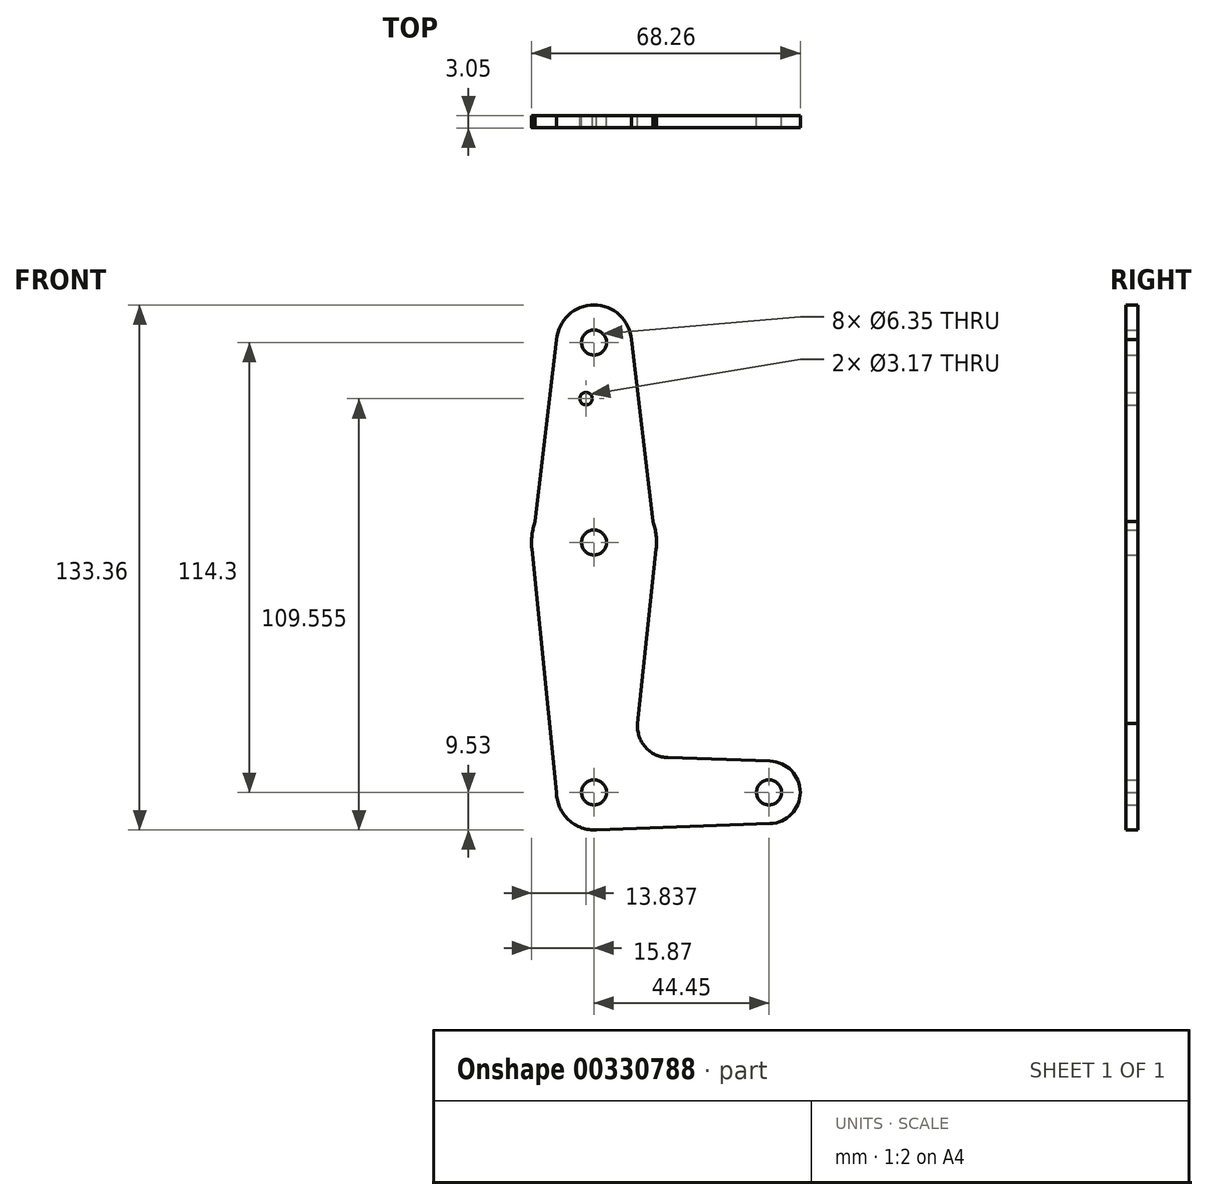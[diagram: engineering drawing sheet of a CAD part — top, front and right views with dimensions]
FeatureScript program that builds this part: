
annotation { "Feature Type Name" : "Feature", "Feature Type Description" : "" }
export const myFeature = defineFeature(function(context is Context, id is Id, definition is map)
    precondition{}
    {
        {
            var Q0;
            Q0=qCreatedBy(makeId("Front.planeOp"),FACE);
            var sketch = newSketch(context, id + "F0", { "sketchPlane" : qUnion([Q0])});
            skLineSegment(sketch, "E0", {"start": v(0, 0) * mm, "end": v(0, 114.3) * mm, "construction": true});
            skLineSegment(sketch, "E1", {"start": v(0, 0) * mm, "end": v(44.45, 0) * mm, "construction": true});
            skCircle(sketch, "E2", {"center": v(0, 114.3) * mm, "radius": 9.53 * mm});
            skCircle(sketch, "E3", {"center": v(0, 63.5) * mm, "radius": 15.88 * mm});
            skCircle(sketch, "E4", {"center": v(0, 0) * mm, "radius": 9.53 * mm});
            skCircle(sketch, "E5", {"center": v(44.45, 0) * mm, "radius": 7.94 * mm});
            skLineSegment(sketch, "E6", {"start": v(-9.5, 115.03) * mm, "end": v(-15.8, 61.88) * mm});
            skLineSegment(sketch, "E7", {"start": v(18.73, 8.81) * mm, "end": v(44.72, 7.93) * mm});
            skLineSegment(sketch, "E8", {"start": v(0, -9.53) * mm, "end": v(44.73, -7.93) * mm});
            skCircle(sketch, "E9", {"center": v(0, 114.3) * mm, "radius": 3.18 * mm});
            skCircle(sketch, "E10", {"center": v(0, 63.5) * mm, "radius": 3.18 * mm});
            skCircle(sketch, "E11", {"center": v(0, 0) * mm, "radius": 3.18 * mm});
            skCircle(sketch, "E12", {"center": v(44.45, 0) * mm, "radius": 3.18 * mm});
            skCircle(sketch, "E13", {"center": v(-2.03, 100.03) * mm, "radius": 1.59 * mm});
            skArc(sketch, "E14.filletArc", {"start": v(11.08, 17.45) * mm, "mid": v(13.05, 11.49) * mm, "end": v(18.73, 8.81) * mm});
            skLineSegment(sketch, "E15", {"start": v(9.5, 115.03) * mm, "end": v(15.8, 61.88) * mm});
            skLineSegment(sketch, "E16", {"start": v(11.08, 17.45) * mm, "end": v(15.8, 61.88) * mm});
            skLineSegment(sketch, "E17", {"start": v(-15.8, 61.88) * mm, "end": v(-9.53, 0) * mm});
            skSolve(sketch);
        }
        {
            var Q0;
            Q0 = qSketchRegion(id + "F0", true);
            extrude(context, id + "F1", {"entities" : qUnion([Q0]), "depth" : 3.05 * mm});
        }
        {
            var Q0;
            Q0 = qSketchRegion(id + "F0", true);
            extrude(context, id + "F2", {"entities" : qUnion([Q0]), "depth" : 3.05 * mm});
        }
    });
